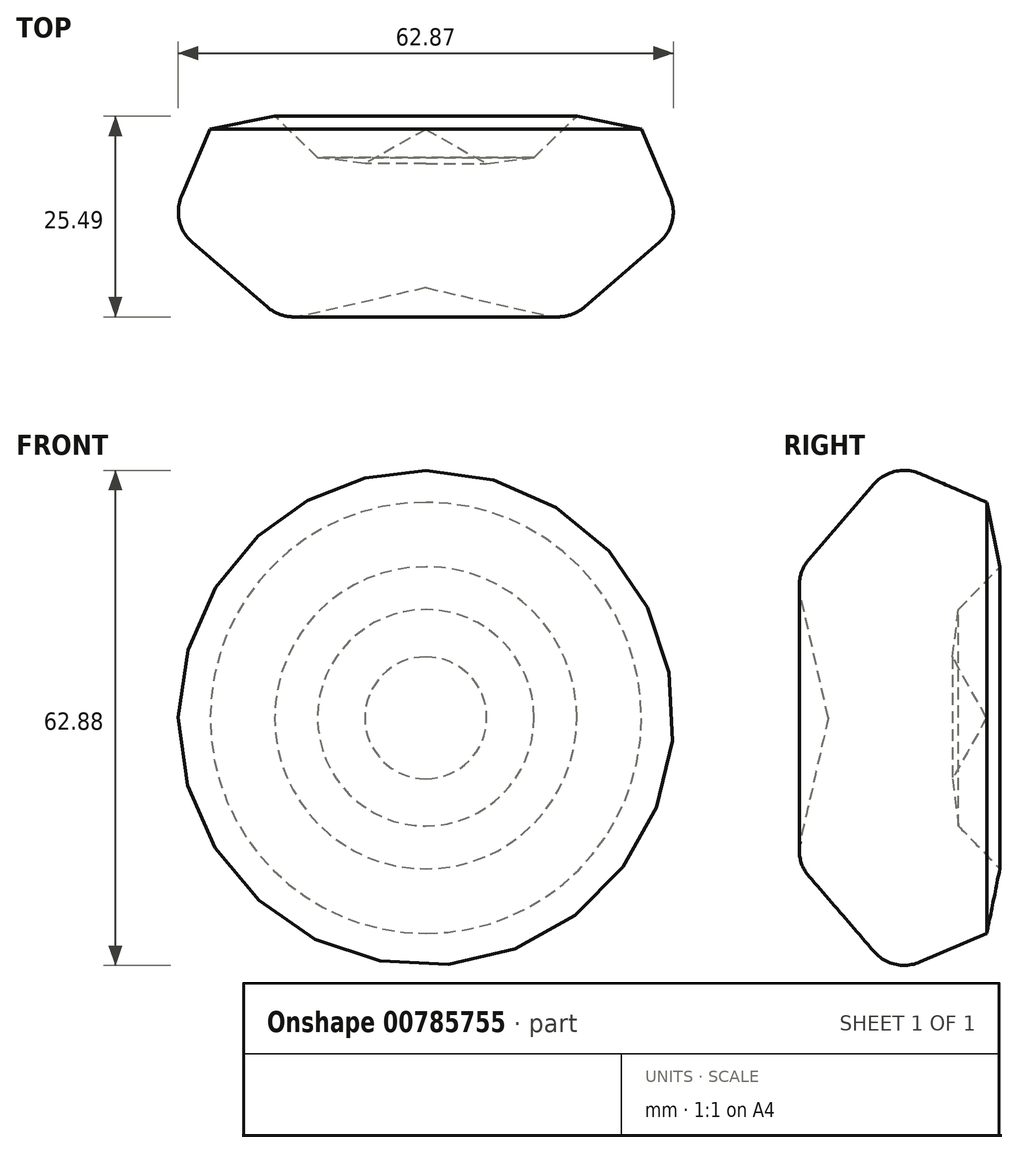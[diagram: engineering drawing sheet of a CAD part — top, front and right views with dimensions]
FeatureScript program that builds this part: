
annotation { "Feature Type Name" : "Feature", "Feature Type Description" : "" }
export const myFeature = defineFeature(function(context is Context, id is Id, definition is map)
    precondition{}
    {
        {
            var Q0;
            Q0=qCreatedBy(makeId("Top.planeOp"),FACE);
            var sketch = newSketch(context, id + "F0", { "sketchPlane" : qUnion([Q0])});
            skLineSegment(sketch, "E0", {"start": v(0, 0) * mm, "end": v(13.46, 12.97) * mm});
            skLineSegment(sketch, "E1", {"start": v(13.46, 12.97) * mm, "end": v(21.46, -5.7) * mm});
            skLineSegment(sketch, "E2", {"start": v(21.46, -5.7) * mm, "end": v(7.15, -18.06) * mm});
            skLineSegment(sketch, "E3", {"start": v(7.15, -18.06) * mm, "end": v(-11.03, -13.93) * mm});
            skLineSegment(sketch, "E4", {"start": v(-11.03, -13.93) * mm, "end": v(-11.03, 6.18) * mm});
            skLineSegment(sketch, "E5", {"start": v(0, 0) * mm, "end": v(-11.03, 6.18) * mm});
            skSolve(sketch);
        }
        {
            var Q0;
            Q0 = qSketchRegion(id + "F0", true);
            var Q1;
            Q1=sQuery(id+"F0.wireOp",EDGE,"E4");
            revolve(context, id + "F1", {"surfaceOperationType" : NewSurfaceOperationType.NEW, "entities" : qUnion([Q0]), "axis" : qUnion([Q1]), "revolveType" : RevolveType.FULL});
        }
        {
            var Q0;
            Q0=makeQuery(id+"F1.opRevolve","SWEPT_FACE",FACE,{"disambiguationData":[OSD([sQuery(id+"F0.wireOp",EDGE,"E2")])]});
            fillet(context, id + "F2", {"entities" : qUnion([Q0]), "tangentPropagation" : true, "radius" : 5.08 * mm, "defaultsChanged" : false, "vertexSettings" : [], "allowEdgeOverflow" : false});
        }
        {
            var Q0;
            Q0=makeQuery(id+"F1.opRevolve","SWEPT_FACE",FACE,{"disambiguationData":[OSD([sQuery(id+"F0.wireOp",EDGE,"E1")])]});
            var Q1;
            Q1=makeQuery(id+"F1.opRevolve","SWEPT_FACE",FACE,{"disambiguationData":[OSD([sQuery(id+"F0.wireOp",EDGE,"E5")])]});
            chamfer(context, id + "F3", {"entities" : qUnion([Q0, Q1]), "width" : 5.08 * mm, "tangentPropagation" : true});
        }
    });
